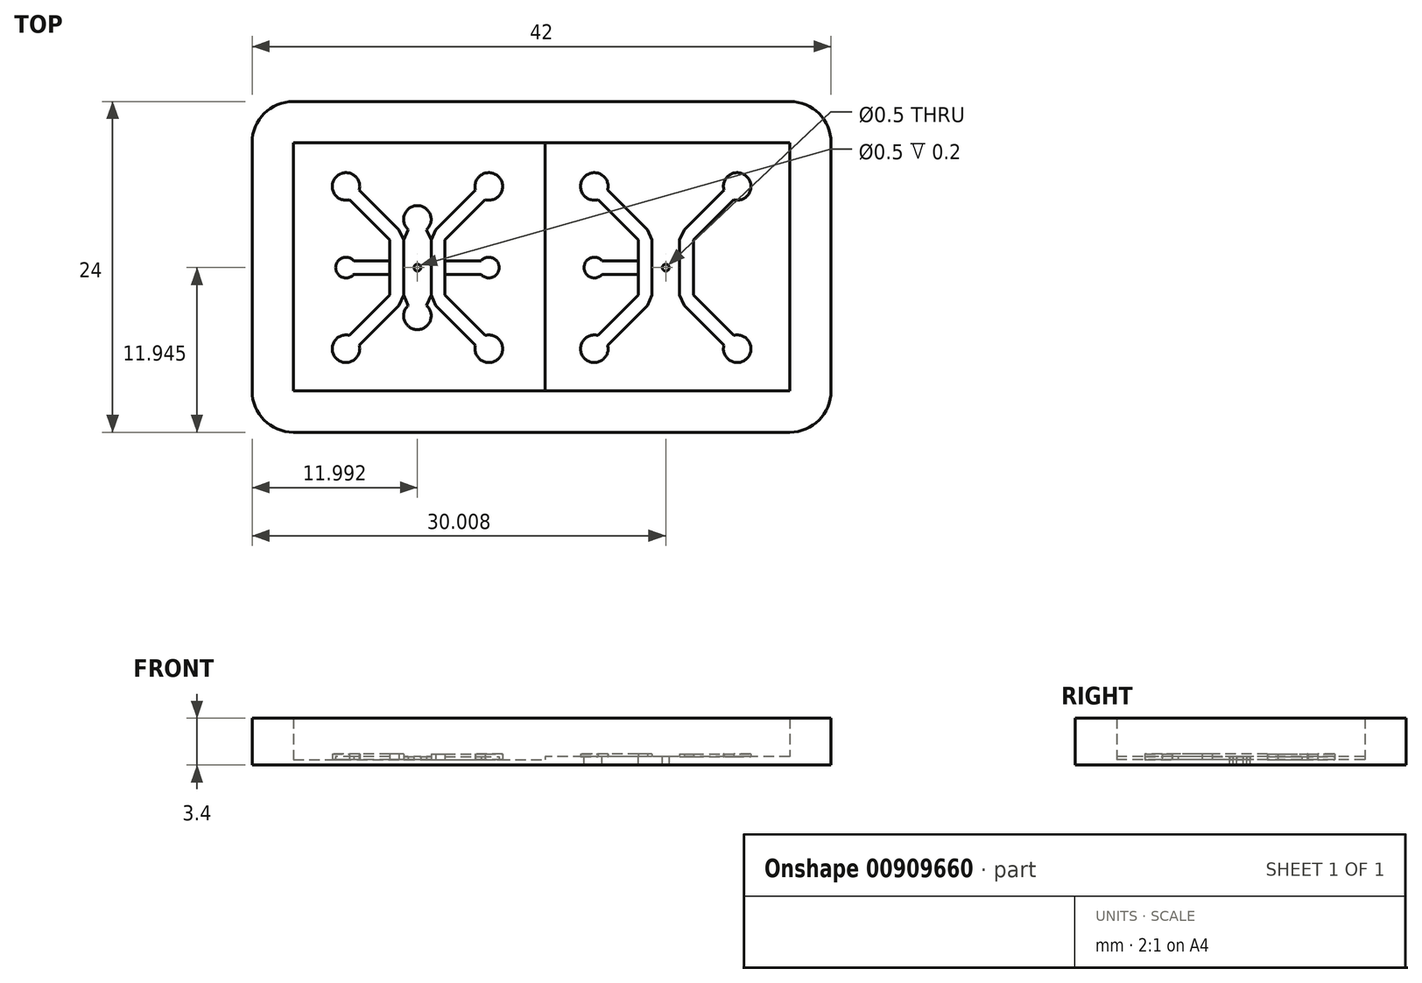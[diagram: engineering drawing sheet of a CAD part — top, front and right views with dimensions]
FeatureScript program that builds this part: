
annotation { "Feature Type Name" : "Feature", "Feature Type Description" : "" }
export const myFeature = defineFeature(function(context is Context, id is Id, definition is map)
    precondition{}
    {
        {
            var Q0;
            Q0=qCreatedBy(makeId("Top.planeOp"),FACE);
            var sketch = newSketch(context, id + "F0", { "sketchPlane" : qUnion([Q0])});
            skLineSegment(sketch, "E0.right", {"start": v(10, 8.95) * mm, "end": v(10, 10.95) * mm});
            skLineSegment(sketch, "E1.MirrorCS", {"start": v(8, 8.95) * mm, "end": v(8, 10.95) * mm});
            skLineSegment(sketch, "E2.MirrorCS", {"start": v(10, 8.95) * mm, "end": v(10, 6.95) * mm});
            skLineSegment(sketch, "E3.MirrorCS", {"start": v(8, 8.95) * mm, "end": v(8, 6.95) * mm});
            skLineSegment(sketch, "E4", {"start": v(9.65, 6.2) * mm, "end": v(10, 6.95) * mm});
            skLineSegment(sketch, "E5", {"start": v(8, 6.95) * mm, "end": v(8.33, 6.2) * mm});
            skCircle(sketch, "E6", {"center": v(9, 8.95) * mm, "radius": 0.25 * mm});
            skArc(sketch, "E7", {"start": v(8.33, 6.2) * mm, "mid": v(9, 4.45) * mm, "end": v(9.65, 6.2) * mm});
            skLineSegment(sketch, "E8.left", {"start": v(10, 10.95) * mm, "end": v(10, 8.95) * mm});
            skLineSegment(sketch, "E8.right", {"start": v(11, 10.95) * mm, "end": v(11, 8.95) * mm});
            skLineSegment(sketch, "E9.MirrorCS", {"start": v(11, 6.95) * mm, "end": v(11, 8.95) * mm});
            skLineSegment(sketch, "E10", {"start": v(10, 6.95) * mm, "end": v(10.33, 6.2) * mm});
            skLineSegment(sketch, "E11", {"start": v(10.33, 6.2) * mm, "end": v(11, 5.53) * mm});
            skLineSegment(sketch, "E12", {"start": v(11, 5.53) * mm, "end": v(13.2, 3.32) * mm});
            skArc(sketch, "E13", {"start": v(13.2, 3.32) * mm, "mid": v(14.88, 2.35) * mm, "end": v(13.92, 4.02) * mm});
            skArc(sketch, "E14.MirrorCS", {"start": v(8.33, 11.7) * mm, "mid": v(9, 13.45) * mm, "end": v(9.65, 11.7) * mm});
            skLineSegment(sketch, "E15.MirrorCS", {"start": v(9.65, 11.7) * mm, "end": v(10, 10.95) * mm});
            skLineSegment(sketch, "E16.MirrorCS", {"start": v(8, 10.95) * mm, "end": v(8.33, 11.7) * mm});
            skLineSegment(sketch, "E17.MirrorCS", {"start": v(10, 10.95) * mm, "end": v(10.33, 11.7) * mm});
            skLineSegment(sketch, "E18.MirrorCS", {"start": v(10.33, 11.7) * mm, "end": v(11, 12.36) * mm});
            skLineSegment(sketch, "E19.MirrorCS", {"start": v(11, 12.36) * mm, "end": v(13.2, 14.58) * mm});
            skArc(sketch, "E20.MirrorCS", {"start": v(13.2, 14.58) * mm, "mid": v(14.88, 15.54) * mm, "end": v(13.92, 13.87) * mm});
            skLineSegment(sketch, "E21", {"start": v(11, 6.95) * mm, "end": v(13.92, 4.02) * mm});
            skLineSegment(sketch, "E22.MirrorCS", {"start": v(11, 10.95) * mm, "end": v(13.92, 13.87) * mm});
            skLineSegment(sketch, "E23.MirrorCS", {"start": v(8, 10.95) * mm, "end": v(7.65, 11.7) * mm});
            skLineSegment(sketch, "E24.MirrorCS", {"start": v(8, 6.95) * mm, "end": v(7.65, 6.2) * mm});
            skLineSegment(sketch, "E25.MirrorCS", {"start": v(7.65, 11.7) * mm, "end": v(7, 12.36) * mm});
            skLineSegment(sketch, "E26.MirrorCS", {"start": v(7, 12.36) * mm, "end": v(4.78, 14.58) * mm});
            skArc(sketch, "E27.MirrorCS", {"start": v(4.78, 14.58) * mm, "mid": v(3.1, 15.54) * mm, "end": v(4.07, 13.87) * mm});
            skLineSegment(sketch, "E28.MirrorCS", {"start": v(7, 10.95) * mm, "end": v(4.07, 13.87) * mm});
            skLineSegment(sketch, "E29.MirrorCS", {"start": v(7, 10.95) * mm, "end": v(7, 8.95) * mm});
            skLineSegment(sketch, "E30.MirrorCS", {"start": v(7, 6.95) * mm, "end": v(7, 8.95) * mm});
            skArc(sketch, "E31.MirrorCS", {"start": v(4.78, 3.32) * mm, "mid": v(3.1, 2.35) * mm, "end": v(4.07, 4.02) * mm});
            skLineSegment(sketch, "E32.MirrorCS", {"start": v(7, 6.95) * mm, "end": v(4.07, 4.02) * mm});
            skLineSegment(sketch, "E33.MirrorCS", {"start": v(7, 5.53) * mm, "end": v(4.78, 3.32) * mm});
            skLineSegment(sketch, "E34.MirrorCS", {"start": v(7.65, 6.2) * mm, "end": v(7, 5.53) * mm});
            skLineSegment(sketch, "E35", {"start": v(11, 9.45) * mm, "end": v(13.61, 9.45) * mm});
            skLineSegment(sketch, "E36", {"start": v(11, 8.45) * mm, "end": v(13.61, 8.45) * mm});
            skArc(sketch, "E37", {"start": v(13.8, 9.6) * mm, "mid": v(13.7, 9.53) * mm, "end": v(13.61, 9.45) * mm});
            skArc(sketch, "E38", {"start": v(13.61, 8.45) * mm, "mid": v(14.91, 8.82) * mm, "end": v(13.8, 9.6) * mm});
            skLineSegment(sketch, "E39.MirrorCS", {"start": v(7, 9.45) * mm, "end": v(4.37, 9.45) * mm});
            skLineSegment(sketch, "E40.MirrorCS", {"start": v(7, 8.45) * mm, "end": v(4.37, 8.45) * mm});
            skArc(sketch, "E41.MirrorCS", {"start": v(4.37, 8.45) * mm, "mid": v(3.07, 8.82) * mm, "end": v(4.18, 9.6) * mm});
            skArc(sketch, "E42.MirrorCS", {"start": v(4.18, 9.6) * mm, "mid": v(4.28, 9.53) * mm, "end": v(4.37, 9.45) * mm});
            skPoint(sketch, "E43.startSnap0", {"position": v(15, 8.95) * mm});
            skPoint(sketch, "E43.startSnap1", {"position": v(14.91, 8.82) * mm});
            skPoint(sketch, "E43.endSnap0", {"position": v(14.91, 8.82) * mm});
            skPoint(sketch, "E44.visualSharp", {"position": v(0, 18) * mm});
            skPoint(sketch, "E45.visualSharp", {"position": v(0, 0) * mm});
            skLineSegment(sketch, "E46", {"start": v(9, 12.45) * mm, "end": v(9, 5.45) * mm});
            skLineSegment(sketch, "E47.bottom", {"start": v(0, 18) * mm, "end": v(18, 18) * mm});
            skLineSegment(sketch, "E47.top", {"start": v(0, 0) * mm, "end": v(18, 0) * mm});
            skLineSegment(sketch, "E47.left", {"start": v(0, 18) * mm, "end": v(0, 0) * mm});
            skLineSegment(sketch, "E47.right", {"start": v(18, 18) * mm, "end": v(18, 0) * mm});
            skLineSegment(sketch, "E48", {"start": v(21.4, 0) * mm, "end": v(21.4, 0) * mm});
            skLineSegment(sketch, "E49.MirrorCS", {"start": v(36, 18) * mm, "end": v(36, 0) * mm});
            skPoint(sketch, "E50.MirrorP", {"position": v(36, 0) * mm});
            skLineSegment(sketch, "E51.MirrorCS", {"start": v(36, 18) * mm, "end": v(18, 18) * mm});
            skPoint(sketch, "E52.MirrorP", {"position": v(36, 18) * mm});
            skLineSegment(sketch, "E53.MirrorCS", {"start": v(14.6, 0) * mm, "end": v(14.6, 0) * mm});
            skLineSegment(sketch, "E54.MirrorCS", {"start": v(36, 0) * mm, "end": v(18, 0) * mm});
            skPoint(sketch, "E55.MirrorP", {"position": v(21.09, 8.82) * mm});
            skLineSegment(sketch, "E56.MirrorCS", {"start": v(28, 10.95) * mm, "end": v(27.67, 11.7) * mm});
            skLineSegment(sketch, "E57.MirrorCS", {"start": v(26, 6.95) * mm, "end": v(25.67, 6.2) * mm});
            skLineSegment(sketch, "E58.MirrorCS", {"start": v(26, 8.95) * mm, "end": v(26, 10.95) * mm});
            skLineSegment(sketch, "E59.MirrorCS", {"start": v(28.35, 6.2) * mm, "end": v(29, 5.53) * mm});
            skArc(sketch, "E60.MirrorCS", {"start": v(31.82, 9.6) * mm, "mid": v(31.72, 9.53) * mm, "end": v(31.63, 9.45) * mm});
            skArc(sketch, "E61.MirrorCS", {"start": v(22.2, 9.6) * mm, "mid": v(22.3, 9.53) * mm, "end": v(22.39, 9.45) * mm});
            skLineSegment(sketch, "E62.MirrorCS", {"start": v(25.67, 11.7) * mm, "end": v(25, 12.36) * mm});
            skLineSegment(sketch, "E63.MirrorCS", {"start": v(28, 10.95) * mm, "end": v(28.35, 11.7) * mm});
            skLineSegment(sketch, "E64.MirrorCS", {"start": v(26, 10.95) * mm, "end": v(25.67, 11.7) * mm});
            skLineSegment(sketch, "E65.MirrorCS", {"start": v(26.35, 11.7) * mm, "end": v(26, 10.95) * mm});
            skLineSegment(sketch, "E66.MirrorCS", {"start": v(28.35, 11.7) * mm, "end": v(29, 12.36) * mm});
            skLineSegment(sketch, "E67.MirrorCS", {"start": v(25.67, 6.2) * mm, "end": v(25, 5.53) * mm});
            skLineSegment(sketch, "E68.MirrorCS", {"start": v(28, 6.95) * mm, "end": v(27.67, 6.2) * mm});
            skLineSegment(sketch, "E69.MirrorCS", {"start": v(28, 6.95) * mm, "end": v(28.35, 6.2) * mm});
            skArc(sketch, "E70.MirrorCS", {"start": v(22.39, 8.45) * mm, "mid": v(21.09, 8.82) * mm, "end": v(22.2, 9.6) * mm});
            skLineSegment(sketch, "E71.MirrorCS", {"start": v(26.35, 6.2) * mm, "end": v(26, 6.95) * mm});
            skPoint(sketch, "E72.MirrorP", {"position": v(21, 8.95) * mm});
            skCircle(sketch, "E73.MirrorC", {"center": v(27, 8.95) * mm, "radius": 0.25 * mm});
            skLineSegment(sketch, "E74.MirrorCS", {"start": v(28, 8.95) * mm, "end": v(28, 10.95) * mm});
            skArc(sketch, "E75.MirrorCS", {"start": v(22.8, 14.58) * mm, "mid": v(21.12, 15.54) * mm, "end": v(22.08, 13.87) * mm});
            skLineSegment(sketch, "E76.MirrorCS", {"start": v(29, 9.45) * mm, "end": v(31.63, 9.45) * mm});
            skLineSegment(sketch, "E77.MirrorCS", {"start": v(29, 6.95) * mm, "end": v(31.93, 4.02) * mm});
            skLineSegment(sketch, "E78.MirrorCS", {"start": v(25, 5.53) * mm, "end": v(22.8, 3.32) * mm});
            skLineSegment(sketch, "E79.MirrorCS", {"start": v(27, 12.45) * mm, "end": v(27, 5.45) * mm});
            skLineSegment(sketch, "E80.MirrorCS", {"start": v(29, 12.36) * mm, "end": v(31.22, 14.58) * mm});
            skLineSegment(sketch, "E81.MirrorCS", {"start": v(29, 6.95) * mm, "end": v(29, 8.95) * mm});
            skLineSegment(sketch, "E82.MirrorCS", {"start": v(29, 5.53) * mm, "end": v(31.22, 3.32) * mm});
            skLineSegment(sketch, "E83.MirrorCS", {"start": v(29, 8.45) * mm, "end": v(31.63, 8.45) * mm});
            skLineSegment(sketch, "E84.MirrorCS", {"start": v(29, 10.95) * mm, "end": v(29, 8.95) * mm});
            skLineSegment(sketch, "E85.MirrorCS", {"start": v(25, 12.36) * mm, "end": v(22.8, 14.58) * mm});
            skLineSegment(sketch, "E86.MirrorCS", {"start": v(26, 10.95) * mm, "end": v(26, 8.95) * mm});
            skArc(sketch, "E87.MirrorCS", {"start": v(31.63, 8.45) * mm, "mid": v(32.93, 8.82) * mm, "end": v(31.82, 9.6) * mm});
            skLineSegment(sketch, "E88.MirrorCS", {"start": v(29, 10.95) * mm, "end": v(31.93, 13.87) * mm});
            skLineSegment(sketch, "E89.MirrorCS", {"start": v(28, 8.95) * mm, "end": v(28, 6.95) * mm});
            skLineSegment(sketch, "E90.MirrorCS", {"start": v(25, 6.95) * mm, "end": v(25, 8.95) * mm});
            skArc(sketch, "E91.MirrorCS", {"start": v(22.8, 3.32) * mm, "mid": v(21.12, 2.35) * mm, "end": v(22.08, 4.02) * mm});
            skLineSegment(sketch, "E92.MirrorCS", {"start": v(25, 10.95) * mm, "end": v(22.08, 13.87) * mm});
            skArc(sketch, "E93.MirrorCS", {"start": v(31.22, 14.58) * mm, "mid": v(32.9, 15.54) * mm, "end": v(31.93, 13.87) * mm});
            skLineSegment(sketch, "E94.MirrorCS", {"start": v(26, 8.95) * mm, "end": v(26, 6.95) * mm});
            skArc(sketch, "E95.MirrorCS", {"start": v(31.22, 3.32) * mm, "mid": v(32.9, 2.35) * mm, "end": v(31.93, 4.02) * mm});
            skLineSegment(sketch, "E96.MirrorCS", {"start": v(25, 10.95) * mm, "end": v(25, 8.95) * mm});
            skArc(sketch, "E97.MirrorCS", {"start": v(27.67, 11.7) * mm, "mid": v(27, 13.45) * mm, "end": v(26.35, 11.7) * mm});
            skLineSegment(sketch, "E98.MirrorCS", {"start": v(25, 8.45) * mm, "end": v(22.39, 8.45) * mm});
            skLineSegment(sketch, "E99.MirrorCS", {"start": v(25, 9.45) * mm, "end": v(22.39, 9.45) * mm});
            skLineSegment(sketch, "E100.MirrorCS", {"start": v(25, 6.95) * mm, "end": v(22.08, 4.02) * mm});
            skArc(sketch, "E101.MirrorCS", {"start": v(27.67, 6.2) * mm, "mid": v(27, 4.45) * mm, "end": v(26.35, 6.2) * mm});
            skLineSegment(sketch, "E102", {"start": v(17.75, 18) * mm, "end": v(17.75, 0) * mm});
            skLineSegment(sketch, "E103.MirrorCS", {"start": v(18.25, 18) * mm, "end": v(18.25, 0) * mm});
            skArc(sketch, "E104", {"start": v(0, 21) * mm, "mid": v(-2.12, 20.12) * mm, "end": v(-3, 18) * mm});
            skLineSegment(sketch, "E105", {"start": v(0, 21) * mm, "end": v(36, 21) * mm});
            skLineSegment(sketch, "E106", {"start": v(39, 18) * mm, "end": v(39, 18) * mm});
            skLineSegment(sketch, "E107", {"start": v(36, -3) * mm, "end": v(0, -3) * mm});
            skLineSegment(sketch, "E108", {"start": v(-3, 18) * mm, "end": v(-3, 0) * mm});
            skLineSegment(sketch, "E109", {"start": v(39, 18) * mm, "end": v(39, 0) * mm});
            skArc(sketch, "E110", {"start": v(36, -3) * mm, "mid": v(38.12, -2.12) * mm, "end": v(39, 0) * mm});
            skArc(sketch, "E111", {"start": v(39, 18) * mm, "mid": v(38.12, 20.12) * mm, "end": v(36, 21) * mm});
            skArc(sketch, "E112", {"start": v(-3, 0) * mm, "mid": v(-2.12, -2.12) * mm, "end": v(0, -3) * mm});
            skSolve(sketch);
        }
        {
            var Q0;
            {var subQ0=sQuery(id+"F0.wireOp",EDGE,"E39.MirrorCS");Q0=makeQuery(id+"F0.imprint","IMPRINT",FACE,{"disambiguationData":[TD([[makeQuery(id+"F0.imprint","IMPRINT",EDGE,{"derivedFrom":subQ0}),1.0]])]});}
            var Q1;
            Q1=makeQuery(id+"F0.imprint","IMPRINT",FACE,{"disambiguationData":[TD([[makeQuery(id+"F0.imprint","IMPRINT",EDGE,{"derivedFrom":sQuery(id+"F0.wireOp",EDGE,"E56.MirrorCS")}),1.0]])]});
            var Q2;
            Q2=makeQuery(id+"F0.imprint","IMPRINT",FACE,{"disambiguationData":[TD([[makeQuery(id+"F0.imprint","IMPRINT",EDGE,{"derivedFrom":sQuery(id+"F0.wireOp",EDGE,"E4")}),-1.0]])]});
            var Q3;
            Q3=makeQuery(id+"F0.imprint","IMPRINT",FACE,{"disambiguationData":[TD([[makeQuery(id+"F0.imprint","IMPRINT",EDGE,{"derivedFrom":sQuery(id+"F0.wireOp",EDGE,"E60.MirrorCS")}),1.0]])]});
            var Q4;
            Q4=makeQuery(id+"F0.imprint","IMPRINT",FACE,{"disambiguationData":[TD([[makeQuery(id+"F0.imprint","IMPRINT",EDGE,{"derivedFrom":sQuery(id+"F0.wireOp",EDGE,"E61.MirrorCS")}),-1.0]])]});
            var Q5;
            Q5=makeQuery(id+"F0.imprint","IMPRINT",FACE,{"disambiguationData":[TD([[makeQuery(id+"F0.imprint","IMPRINT",EDGE,{"derivedFrom":sQuery(id+"F0.wireOp",EDGE,"E57.MirrorCS")}),-1.0]])]});
            var Q6;
            {var subQ1=sQuery(id+"F0.wireOp",EDGE,"E49.MirrorCS");Q6=makeQuery(id+"F0.imprint","IMPRINT",FACE,{"disambiguationData":[TD([[makeQuery(id+"F0.imprint","IMPRINT",EDGE,{"derivedFrom":subQ1}),-1.0]])]});}
            var Q7;
            Q7=makeQuery(id+"F0.imprint","IMPRINT",FACE,{"disambiguationData":[TD([[makeQuery(id+"F0.imprint","IMPRINT",EDGE,{"derivedFrom":sQuery(id+"F0.wireOp",EDGE,"E59.MirrorCS")}),1.0]])]});
            var Q8;
            Q8=makeQuery(id+"F0.imprint","IMPRINT",FACE,{"disambiguationData":[TD([[makeQuery(id+"F0.imprint","IMPRINT",EDGE,{"derivedFrom":sQuery(id+"F0.wireOp",EDGE,"E1.MirrorCS")}),1.0]])]});
            var Q9;
            Q9=makeQuery(id+"F0.imprint","IMPRINT",FACE,{"disambiguationData":[TD([[makeQuery(id+"F0.imprint","IMPRINT",EDGE,{"derivedFrom":sQuery(id+"F0.wireOp",EDGE,"E2.MirrorCS")}),1.0]])]});
            var Q10;
            Q10=makeQuery(id+"F0.imprint","IMPRINT",FACE,{"disambiguationData":[TD([[makeQuery(id+"F0.imprint","IMPRINT",EDGE,{"derivedFrom":sQuery(id+"F0.wireOp",EDGE,"E1.MirrorCS")}),-1.0]])]});
            var Q11;
            {var subQ4=sQuery(id+"F0.wireOp",EDGE,"E35");Q11=makeQuery(id+"F0.imprint","IMPRINT",FACE,{"disambiguationData":[TD([[makeQuery(id+"F0.imprint","IMPRINT",EDGE,{"derivedFrom":subQ4}),-1.0]])]});}
            var Q12;
            {var subQ3=sQuery(id+"F0.wireOp",EDGE,"E102");Q12=makeQuery(id+"F0.imprint","IMPRINT",FACE,{"disambiguationData":[TD([[makeQuery(id+"F0.imprint","IMPRINT",EDGE,{"derivedFrom":subQ3}),1.0]])]});}
            var Q13;
            {var subQ5=sQuery(id+"F0.wireOp",EDGE,"E103.MirrorCS");Q13=makeQuery(id+"F0.imprint","IMPRINT",FACE,{"disambiguationData":[TD([[makeQuery(id+"F0.imprint","IMPRINT",EDGE,{"derivedFrom":subQ5}),-1.0]])]});}
            var Q14;
            {var subQ0=sQuery(id+"F0.wireOp",EDGE,"E46");var subQ1=sQuery(id+"F0.wireOp",EDGE,"E6");var subQ2=makeQuery(id+"F0.imprint","INTERSECT",VERTEX,{"disambiguationData":[OD(0.0)],"derivedFrom":[subQ1,subQ0]});Q14=makeQuery(id+"F0.imprint","IMPRINT",FACE,{"disambiguationData":[TD([[makeQuery(id+"F0.imprint","IMPRINT",EDGE,{"disambiguationData":[TD([[subQ2,1.0]])],"derivedFrom":subQ1}),1.0]])]});}
            var Q15;
            {var subQ0=sQuery(id+"F0.wireOp",EDGE,"E79.MirrorCS");var subQ1=sQuery(id+"F0.wireOp",EDGE,"E73.MirrorC");var subQ2=makeQuery(id+"F0.imprint","INTERSECT",VERTEX,{"disambiguationData":[OD(0.0)],"derivedFrom":[subQ1,subQ0]});Q15=makeQuery(id+"F0.imprint","IMPRINT",FACE,{"disambiguationData":[TD([[makeQuery(id+"F0.imprint","IMPRINT",EDGE,{"disambiguationData":[TD([[subQ2,1.0]])],"derivedFrom":subQ1}),-1.0]])]});}
            var Q16;
            {var subQ0=sQuery(id+"F0.wireOp",EDGE,"E46");var subQ1=sQuery(id+"F0.wireOp",EDGE,"E6");var subQ2=makeQuery(id+"F0.imprint","INTERSECT",VERTEX,{"disambiguationData":[OD(0.0)],"derivedFrom":[subQ1,subQ0]});Q16=makeQuery(id+"F0.imprint","IMPRINT",FACE,{"disambiguationData":[TD([[makeQuery(id+"F0.imprint","IMPRINT",EDGE,{"disambiguationData":[TD([[subQ2,-1.0]])],"derivedFrom":subQ1}),1.0]])]});}
            var Q17;
            {var subQ0=sQuery(id+"F0.wireOp",EDGE,"E79.MirrorCS");var subQ1=sQuery(id+"F0.wireOp",EDGE,"E73.MirrorC");var subQ2=makeQuery(id+"F0.imprint","INTERSECT",VERTEX,{"disambiguationData":[OD(0.0)],"derivedFrom":[subQ1,subQ0]});Q17=makeQuery(id+"F0.imprint","IMPRINT",FACE,{"disambiguationData":[TD([[makeQuery(id+"F0.imprint","IMPRINT",EDGE,{"disambiguationData":[TD([[subQ2,-1.0]])],"derivedFrom":subQ1}),-1.0]])]});}
            var Q18;
            {var subQ0=sQuery(id+"F0.wireOp",EDGE,"E51.MirrorCS");var subQ1=sQuery(id+"F0.wireOp",EDGE,"E47.bottom");var subQ2=makeQuery(id+"F0.imprint","INTERSECT",VERTEX,{"derivedFrom":[subQ1,sQuery(id+"F0.wireOp",EDGE,"E47.right"),subQ0]});Q18=makeQuery(id+"F0.imprint","IMPRINT",FACE,{"disambiguationData":[TD([[makeQuery(id+"F0.imprint","IMPRINT",EDGE,{"disambiguationData":[TD([[subQ2,1.0]])],"derivedFrom":subQ1}),1.0]])]});}
            var Q19;
            {var subQ0=sQuery(id+"F0.wireOp",EDGE,"E47.right");var subQ3=sQuery(id+"F0.wireOp",EDGE,"8D0ttMVF-N7t8-bLoh-d2Lt-IWmziKVZ8kqY");var subQ5=makeQuery(id+"F0.imprint","INTERSECT",VERTEX,{"derivedFrom":[subQ0,subQ3]});Q19=makeQuery(id+"F0.imprint","IMPRINT",FACE,{"disambiguationData":[TD([[makeQuery(id+"F0.imprint","IMPRINT",EDGE,{"disambiguationData":[TD([[subQ5,1.0]])],"derivedFrom":subQ0}),-1.0]])]});}
            var Q20;
            {var subQ1=sQuery(id+"F0.wireOp",EDGE,"E47.right");var subQ3=sQuery(id+"F0.wireOp",EDGE,"8D0ttMVF-N7t8-bLoh-d2Lt-IWmziKVZ8kqY");var subQ4=makeQuery(id+"F0.imprint","INTERSECT",VERTEX,{"derivedFrom":[subQ1,subQ3]});Q20=makeQuery(id+"F0.imprint","IMPRINT",FACE,{"disambiguationData":[TD([[makeQuery(id+"F0.imprint","IMPRINT",EDGE,{"disambiguationData":[TD([[subQ4,1.0]])],"derivedFrom":subQ1}),1.0]])]});}
            extrude(context, id + "F1", {"entities" : qUnion([Q0, Q1, Q2, Q3, Q4, Q5, Q6, Q7, Q8, Q9, Q10, Q11, Q12, Q13, Q14, Q15, Q16, Q17, Q18, Q19, Q20]), "depth" : -0.4 * mm, "offsetDistance" : 25 * mm});
        }
        {
            var Q0;
            {var subQ11=sQuery(id+"F0.wireOp",EDGE,"E47.left");Q0=makeQuery(id+"F0.imprint","IMPRINT",FACE,{"disambiguationData":[TD([[makeQuery(id+"F0.imprint","IMPRINT",EDGE,{"derivedFrom":subQ11}),-1.0]])]});}
            extrude(context, id + "F2", {"entities" : qUnion([Q0]), "operationType" : NewBodyOperationType.ADD, "depth" : 3 * mm, "offsetDistance" : 25 * mm});
        }
        {
            var Q0;
            Q0=makeQuery(id+"F0.imprint","IMPRINT",FACE,{"disambiguationData":[TD([[makeQuery(id+"F0.imprint","IMPRINT",EDGE,{"derivedFrom":sQuery(id+"F0.wireOp",EDGE,"E1.MirrorCS")}),1.0]])]});
            var Q1;
            Q1=makeQuery(id+"F0.imprint","IMPRINT",FACE,{"disambiguationData":[TD([[makeQuery(id+"F0.imprint","IMPRINT",EDGE,{"derivedFrom":sQuery(id+"F0.wireOp",EDGE,"E2.MirrorCS")}),1.0]])]});
            var Q2;
            Q2=makeQuery(id+"F0.imprint","IMPRINT",FACE,{"disambiguationData":[TD([[makeQuery(id+"F0.imprint","IMPRINT",EDGE,{"derivedFrom":sQuery(id+"F0.wireOp",EDGE,"E57.MirrorCS")}),-1.0]])]});
            var Q3;
            Q3=makeQuery(id+"F0.imprint","IMPRINT",FACE,{"disambiguationData":[TD([[makeQuery(id+"F0.imprint","IMPRINT",EDGE,{"derivedFrom":sQuery(id+"F0.wireOp",EDGE,"E59.MirrorCS")}),1.0]])]});
            extrude(context, id + "F3", {"entities" : qUnion([Q0, Q1, Q2, Q3]), "operationType" : NewBodyOperationType.ADD, "depth" : .4 * mm, "offsetDistance" : 25 * mm});
        }
        {
            var Q0;
            {var subQ0=sQuery(id+"F0.wireOp",EDGE,"E39.MirrorCS");Q0=makeQuery(id+"F0.imprint","IMPRINT",FACE,{"disambiguationData":[TD([[makeQuery(id+"F0.imprint","IMPRINT",EDGE,{"derivedFrom":subQ0}),1.0]])]});}
            var Q1;
            Q1=makeQuery(id+"F0.imprint","IMPRINT",FACE,{"disambiguationData":[TD([[makeQuery(id+"F0.imprint","IMPRINT",EDGE,{"derivedFrom":sQuery(id+"F0.wireOp",EDGE,"E1.MirrorCS")}),-1.0]])]});
            var Q2;
            {var subQ4=sQuery(id+"F0.wireOp",EDGE,"E35");Q2=makeQuery(id+"F0.imprint","IMPRINT",FACE,{"disambiguationData":[TD([[makeQuery(id+"F0.imprint","IMPRINT",EDGE,{"derivedFrom":subQ4}),-1.0]])]});}
            var Q3;
            Q3=makeQuery(id+"F0.imprint","IMPRINT",FACE,{"disambiguationData":[TD([[makeQuery(id+"F0.imprint","IMPRINT",EDGE,{"derivedFrom":sQuery(id+"F0.wireOp",EDGE,"E61.MirrorCS")}),-1.0]])]});
            var Q4;
            Q4=makeQuery(id+"F0.imprint","IMPRINT",FACE,{"disambiguationData":[TD([[makeQuery(id+"F0.imprint","IMPRINT",EDGE,{"derivedFrom":sQuery(id+"F0.wireOp",EDGE,"E56.MirrorCS")}),1.0]])]});
            var Q5;
            Q5=makeQuery(id+"F0.imprint","IMPRINT",FACE,{"disambiguationData":[TD([[makeQuery(id+"F0.imprint","IMPRINT",EDGE,{"derivedFrom":sQuery(id+"F0.wireOp",EDGE,"E60.MirrorCS")}),1.0]])]});
            extrude(context, id + "F4", {"entities" : qUnion([Q0, Q1, Q2, Q3, Q4, Q5]), "operationType" : NewBodyOperationType.ADD, "depth" : 0.2 * mm, "offsetDistance" : 25 * mm});
        }
    });
